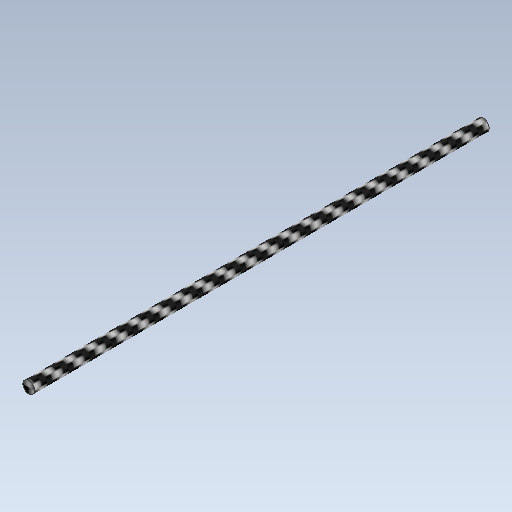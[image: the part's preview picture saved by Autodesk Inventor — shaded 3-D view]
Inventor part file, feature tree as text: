
AUTODESK INVENTOR PART (.ipt)
format: ipt  version: 2020 (Build 240168000, 168)  size: 107,520 bytes
history: native  units: in
note: dims shown in document units (in); Inventor stores cm internally (conversion verified against a paired STEP export)
features: extrude x1, sketch x1
ambient origin geometry x8: Origin, YZ Plane, XZ Plane, XY Plane, X Axis, Y Axis, Z Axis, Center Point
bodies: Solid1 (feature_tree)
feature tree (2):
  extrude  "Extrusion1"  Depth=3.1106in
  sketch  "Sketch1"  dims[d0=0.0827in d1=3.1106in d2=0.0in]
